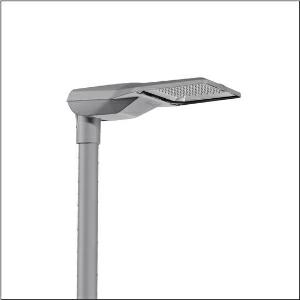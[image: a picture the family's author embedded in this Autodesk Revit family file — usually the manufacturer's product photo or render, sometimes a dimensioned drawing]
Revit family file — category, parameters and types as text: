
# Revit family: streetlight_sl_21_iq_midi___st1_0a_5xe3d41g08nb_8322
name_source: partatom
category: Lighting Fixtures
units: mm (PartAtom-declared; Revit-internal decimal feet)

## family parameters
Cut with Voids When Loaded = No
Host = Face
Light Source = No
Part Type = Normal
Room Calculation Point = No
Round Connector Dimension = Use Diameter
Shared = No

## types (1)
- --- (1 x LED, 24250 lm, 155.5 W, 4000K)
    Apparent Load = 155 VA
    CIE Flux Codes = 40 73 97 100 100
    Color Rendering = 70
    Color Temperature = 4000K
    Default Elevation = 1800 mm
    Description = Streetlight SL 21 iQ midi, mast luminaire, primary light control with lens, of PMMA, primary optical cover: cover, of toughened safety glass, transparent, light distribution: ST1.0a, light emission: direct distribution, primary light characteristic: asymmetric, installation type: post-top, side-entry, LED, High Power LED, rated luminous flux: 24.250lm, luminous efficacy: 156lm/W, light colour: 740, colour temperature: 4000K, control: Street-Remote, Auto-Match, Temp-Guard, Lumen-Switch, Night-Set, Smart-Wire, Light-Fading, Desk-Remote (wireless, voltage-free reading and setting of iQ features in the workshop via application-optimized NFC function/RFID function), optimised constant luminous flux control (CLO 2.0), presetting dimming linear, mains connection: 230..240V, AC, 50/60Hz, start of lifetime: 156W, end of service life: 162W, reduction: 69W, luminaire housing, of diecast aluminium, powder-coated, Siteco® metallic grey (DB 702S), corrosivity category C5 mid according to DIN EN ISO 12944, please order mast flange separately, inclination adjustable: 0°, 5°, 10°, 15°, sealing non-destructively replaceable, multi-level sealing system, length: 644mm, width: 335mm, height: 110mm, mast flange for spigot size: 42mm (side-entry): 5XC10008XM4, 60/48mm (side-entry/post-top): 5XC10108XM2, 76/60mm (side-entry/post-top): 5XC10108XM1, protection rating (complete): IP66, insulation class (complete): insulation class II (safety insulation), certification: CE, ENEC, ENEC+, VDE, impact resistance: IK09, permissible operating ambient temperature for outdoor applications: -40..+50°C, standard-compliant lighting for roads and squares, packaging unit: 1 piece

Light Distribution: ST1.0a
    Height = 111 mm
    Lamp = 1 x LED
    Lamp Light Flux = 24250 lm
    Lamp Power = 155.5 W
    Lamp count = 1
    Length = 644 mm
    Luminous efficacy = 156 lm/W
    Manufacturer = Siteco
    ModVariant = No
    Model = 5XE3D41G08NB
    Number of Poles = 1
    OnlyDefault = Yes
    Power Factor = 1
    Product Name = Streetlight SL 21 iQ midi | ST1.0a
    Product group = mast luminaire | pylon top
    ProductGroupID = 6100
    Protection Class = Protection class II
    Protection Degree = IP 66
    RLX_Detail_Level = 1
    RLX_Emergency_Light_Flux = 0 lm
    RLX_Emergency_Type = 0
    RLX_Emergency_Type_DB = No
    RlxData = <blob elided: 91165 chars, md5=0c0e6fa6>
    Socket = socket
    Standby Power = 0 W
    System Light Flux = 24250 lm
    System Power = 155 W
    Type Comments = factory setting: luminous flux: 100 % | dim-lin: 254 | 823 mA
    Type Image = l_1004298.jpg
    URL = http://relux.com
    VarID = @adj_103503
    Voltage = 0 V
    Weight = 0.00 kg
    Width = 336 mm

## geometry (parser evidence)
native form markers: Blend x4, Sweep x10
no freeform markers — native parametric forms only
